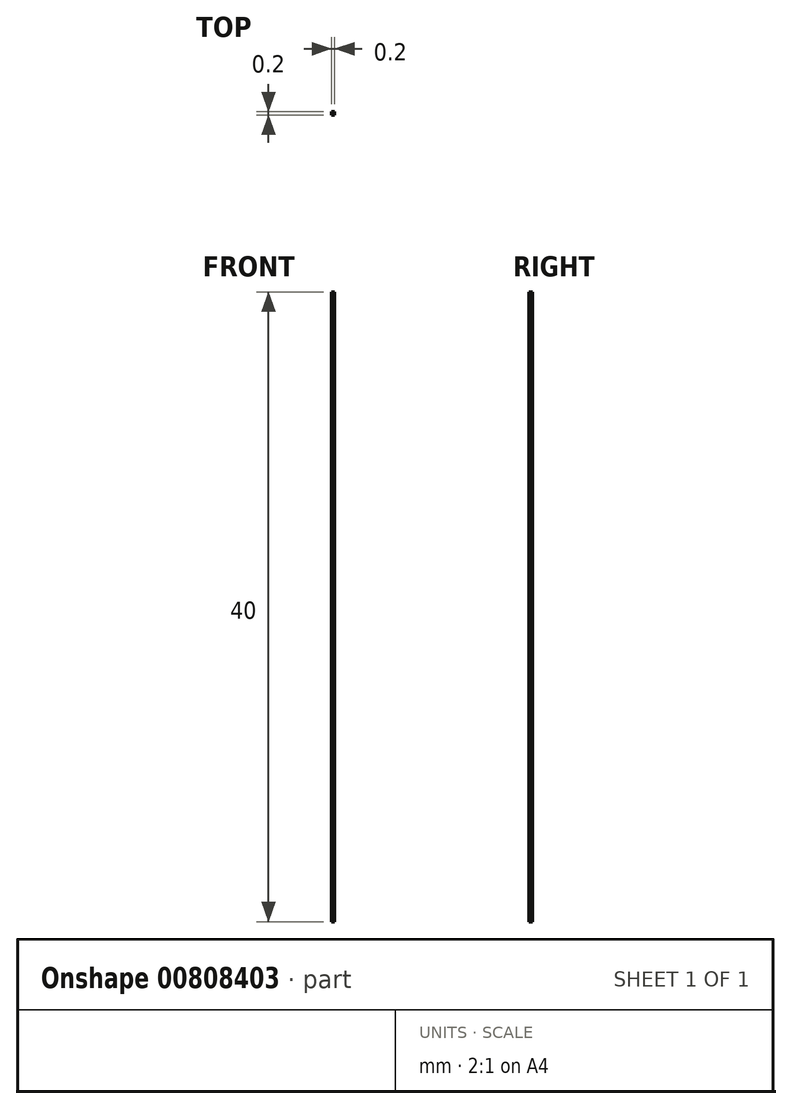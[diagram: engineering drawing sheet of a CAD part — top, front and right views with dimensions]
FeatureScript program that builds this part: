
annotation { "Feature Type Name" : "Feature", "Feature Type Description" : "" }
export const myFeature = defineFeature(function(context is Context, id is Id, definition is map)
    precondition{}
    {
        {
            var Q0;
            Q0=qCreatedBy(makeId("Front.planeOp"),FACE);
            var sketch = newSketch(context, id + "F0", { "sketchPlane" : qUnion([Q0])});
            skLineSegment(sketch, "E0", {"start": v(0, 0) * mm, "end": v(0, 40) * mm});
            skLineSegment(sketch, "E1", {"start": v(0, 40) * mm, "end": v(0.2, 40) * mm});
            skLineSegment(sketch, "E2", {"start": v(0.2, 40) * mm, "end": v(0.2, 0) * mm});
            skLineSegment(sketch, "E3", {"start": v(0.2, 0) * mm, "end": v(0, 0) * mm});
            skSolve(sketch);
        }
        {
            var Q0;
            Q0 = qSketchRegion(id + "F0", true);
            extrude(context, id + "F1", {"entities" : qUnion([Q0]), "depth" : .2 * mm, "offsetDistance" : 25.4 * mm});
        }
    });
